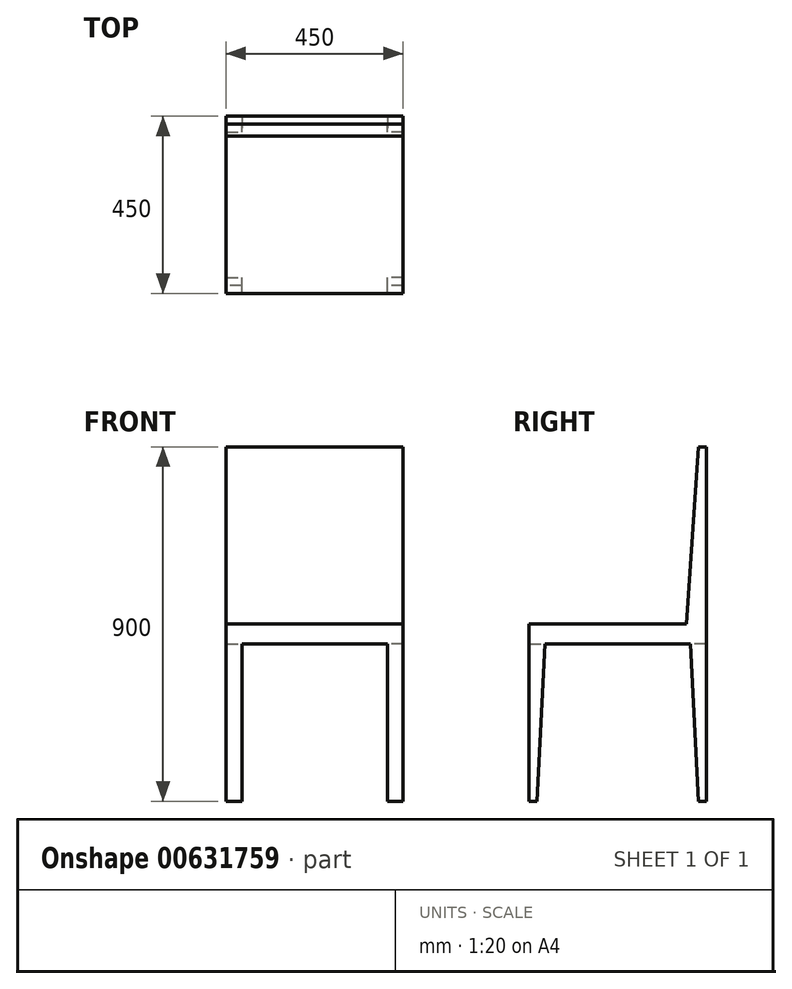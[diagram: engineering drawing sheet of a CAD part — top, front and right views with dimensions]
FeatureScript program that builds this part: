
annotation { "Feature Type Name" : "Feature", "Feature Type Description" : "" }
export const myFeature = defineFeature(function(context is Context, id is Id, definition is map)
    precondition{}
    {
        {
            var Q0;
            Q0=qCreatedBy(makeId("Top.planeOp"),FACE);
            var sketch = newSketch(context, id + "F0", { "sketchPlane" : qUnion([Q0])});
            skLineSegment(sketch, "E0.bottom", {"start": v(0, 0) * mm, "end": v(450, 0) * mm});
            skLineSegment(sketch, "E0.top", {"start": v(0, 450) * mm, "end": v(450, 450) * mm});
            skLineSegment(sketch, "E0.left", {"start": v(0, 0) * mm, "end": v(0, 450) * mm});
            skLineSegment(sketch, "E0.right", {"start": v(450, 0) * mm, "end": v(450, 450) * mm});
            skSolve(sketch);
        }
        {
            var Q0;
            Q0=makeQuery(id+"F0.imprint","IMPRINT",FACE,{"disambiguationData":[TD([[makeQuery(id+"F0.imprint","IMPRINT",EDGE,{"derivedFrom":sQuery(id+"F0.wireOp",EDGE,"E0.bottom")}),1.0]])]});
            extrude(context, id + "F1", {"entities" : qUnion([Q0]), "depth" : 50 * mm, "offsetDistance" : 25 * mm});
        }
        {
            var Q0;
            Q0=makeQuery(id+"F1.opExtrude","CAP_FACE",FACE,{"disambiguationData":[OSD([sQuery(id+"F0.wireOp",EDGE,"E0.bottom"),sQuery(id+"F0.wireOp",EDGE,"E0.top"),sQuery(id+"F0.wireOp",EDGE,"E0.left"),sQuery(id+"F0.wireOp",EDGE,"E0.right")])],"isStart":true});
            var sketch = newSketch(context, id + "F2", { "sketchPlane" : qUnion([Q0])});
            skLineSegment(sketch, "E1.bottom", {"start": v(0, -450) * mm, "end": v(40, -450) * mm});
            skLineSegment(sketch, "E1.top", {"start": v(0, -410) * mm, "end": v(40, -410) * mm});
            skLineSegment(sketch, "E1.left", {"start": v(0, -450) * mm, "end": v(0, -410) * mm});
            skLineSegment(sketch, "E1.right", {"start": v(40, -450) * mm, "end": v(40, -410) * mm});
            skSolve(sketch);
        }
        {
            var Q0;
            Q0=makeQuery(id+"F2.imprint","IMPRINT",FACE,{"disambiguationData":[TD([[makeQuery(id+"F2.imprint","IMPRINT",EDGE,{"derivedFrom":sQuery(id+"F2.wireOp",EDGE,"E1.bottom")}),1.0]])]});
            var Q1;
            Q1=sQuery(id+"F2.wireOp",EDGE,"E1.right");
            extrude(context, id + "F3", {"entities" : qUnion([Q0]), "operationType" : NewBodyOperationType.ADD, "surfaceEntities" : qUnion([Q1]), "depth" : 400 * mm, "offsetDistance" : 25 * mm});
        }
        {
            var Q0;
            Q0=makeQuery(id+"F1.opExtrude","CAP_FACE",FACE,{"disambiguationData":[OSD([sQuery(id+"F0.wireOp",EDGE,"E0.bottom"),sQuery(id+"F0.wireOp",EDGE,"E0.top"),sQuery(id+"F0.wireOp",EDGE,"E0.left"),sQuery(id+"F0.wireOp",EDGE,"E0.right")])],"isStart":true});
            var sketch = newSketch(context, id + "F4", { "sketchPlane" : qUnion([Q0])});
            skLineSegment(sketch, "E2.bottom", {"start": v(0, 0) * mm, "end": v(40, 0) * mm});
            skLineSegment(sketch, "E2.top", {"start": v(0, -40) * mm, "end": v(40, -40) * mm});
            skLineSegment(sketch, "E2.left", {"start": v(0, 0) * mm, "end": v(0, -40) * mm});
            skLineSegment(sketch, "E2.right", {"start": v(40, 0) * mm, "end": v(40, -40) * mm});
            skSolve(sketch);
        }
        {
            var Q0;
            Q0=makeQuery(id+"F4.imprint","IMPRINT",FACE,{"disambiguationData":[TD([[makeQuery(id+"F4.imprint","IMPRINT",EDGE,{"derivedFrom":sQuery(id+"F4.wireOp",EDGE,"E2.bottom")}),-1.0]])]});
            extrude(context, id + "F5", {"entities" : qUnion([Q0]), "operationType" : NewBodyOperationType.ADD, "depth" : 400 * mm, "offsetDistance" : 25 * mm});
        }
        {
            var Q0;
            Q0=makeQuery(id+"F1.opExtrude","CAP_FACE",FACE,{"disambiguationData":[OSD([sQuery(id+"F0.wireOp",EDGE,"E0.bottom"),sQuery(id+"F0.wireOp",EDGE,"E0.top"),sQuery(id+"F0.wireOp",EDGE,"E0.left"),sQuery(id+"F0.wireOp",EDGE,"E0.right")])],"isStart":true});
            var sketch = newSketch(context, id + "F6", { "sketchPlane" : qUnion([Q0])});
            skLineSegment(sketch, "E3.bottom", {"start": v(450, -450) * mm, "end": v(410, -450) * mm});
            skLineSegment(sketch, "E3.top", {"start": v(450, -410) * mm, "end": v(410, -410) * mm});
            skLineSegment(sketch, "E3.left", {"start": v(450, -450) * mm, "end": v(450, -410) * mm});
            skLineSegment(sketch, "E3.right", {"start": v(410, -450) * mm, "end": v(410, -410) * mm});
            skSolve(sketch);
        }
        {
            var Q0;
            Q0=qSketchRegion(id+"F6",true);
            var Q1;
            Q1=makeQuery(id+"F6.imprint","IMPRINT",FACE,{"disambiguationData":[TD([[makeQuery(id+"F6.imprint","IMPRINT",EDGE,{"derivedFrom":sQuery(id+"F6.wireOp",EDGE,"E3.bottom")}),1.0]])]});
            extrude(context, id + "F7", {"entities" : qUnion([Q0, Q1]), "operationType" : NewBodyOperationType.ADD, "depth" : 400 * mm, "offsetDistance" : 25 * mm});
        }
        {
            var Q0;
            Q0=makeQuery(id+"F1.opExtrude","CAP_FACE",FACE,{"disambiguationData":[OSD([sQuery(id+"F0.wireOp",EDGE,"E0.bottom"),sQuery(id+"F0.wireOp",EDGE,"E0.top"),sQuery(id+"F0.wireOp",EDGE,"E0.left"),sQuery(id+"F0.wireOp",EDGE,"E0.right")])],"isStart":true});
            var sketch = newSketch(context, id + "F8", { "sketchPlane" : qUnion([Q0])});
            skLineSegment(sketch, "E4.bottom", {"start": v(450, 0) * mm, "end": v(410, 0) * mm});
            skLineSegment(sketch, "E4.top", {"start": v(450, -40) * mm, "end": v(410, -40) * mm});
            skLineSegment(sketch, "E4.left", {"start": v(450, 0) * mm, "end": v(450, -40) * mm});
            skLineSegment(sketch, "E4.right", {"start": v(410, 0) * mm, "end": v(410, -40) * mm});
            skSolve(sketch);
        }
        {
            var Q0;
            Q0=makeQuery(id+"F8.imprint","IMPRINT",FACE,{"disambiguationData":[TD([[makeQuery(id+"F8.imprint","IMPRINT",EDGE,{"derivedFrom":sQuery(id+"F8.wireOp",EDGE,"E4.bottom")}),-1.0]])]});
            extrude(context, id + "F9", {"entities" : qUnion([Q0]), "operationType" : NewBodyOperationType.ADD, "depth" : 400 * mm, "offsetDistance" : 25 * mm});
        }
        {
            var Q0;
            Q0=makeQuery(id+"F1.opExtrude","CAP_FACE",FACE,{"disambiguationData":[OSD([sQuery(id+"F0.wireOp",EDGE,"E0.bottom"),sQuery(id+"F0.wireOp",EDGE,"E0.top"),sQuery(id+"F0.wireOp",EDGE,"E0.left"),sQuery(id+"F0.wireOp",EDGE,"E0.right")])],"isStart":false});
            var sketch = newSketch(context, id + "F10", { "sketchPlane" : qUnion([Q0])});
            skLineSegment(sketch, "E5.bottom", {"start": v(450, 450) * mm, "end": v(0, 450) * mm});
            skLineSegment(sketch, "E5.top", {"start": v(450, 400) * mm, "end": v(0, 400) * mm});
            skLineSegment(sketch, "E5.left", {"start": v(450, 450) * mm, "end": v(450, 400) * mm});
            skLineSegment(sketch, "E5.right", {"start": v(0, 450) * mm, "end": v(0, 400) * mm});
            skSolve(sketch);
        }
        {
            var Q0;
            Q0=makeQuery(id+"F10.imprint","IMPRINT",FACE,{"disambiguationData":[TD([[makeQuery(id+"F10.imprint","IMPRINT",EDGE,{"derivedFrom":sQuery(id+"F10.wireOp",EDGE,"E5.bottom")}),-1.0]])]});
            extrude(context, id + "F11", {"entities" : qUnion([Q0]), "operationType" : NewBodyOperationType.ADD, "depth" : 450 * mm, "offsetDistance" : 25 * mm});
        }
        {
            var Q0;
            Q0=makeQuery(id+"F11.boolean.opBoolean","MERGE",FACE,{"derivedFrom":[makeQuery(id+"F9.boolean.opBoolean","MERGE",FACE,{"derivedFrom":[makeQuery(id+"F7.boolean.opBoolean","MERGE",FACE,{"derivedFrom":[makeQuery(id+"F1.opExtrude","SWEPT_FACE",FACE,{"disambiguationData":[OSD([sQuery(id+"F0.wireOp",EDGE,"E0.right")])]}),makeQuery(id+"F7.opExtrude","SWEPT_FACE",FACE,{"disambiguationData":[OSD([sQuery(id+"F6.wireOp",EDGE,"E3.left")])]})]}),makeQuery(id+"F9.opExtrude","SWEPT_FACE",FACE,{"disambiguationData":[OSD([sQuery(id+"F8.wireOp",EDGE,"E4.left")])]})]}),makeQuery(id+"F11.opExtrude","SWEPT_FACE",FACE,{"disambiguationData":[OSD([sQuery(id+"F10.wireOp",EDGE,"E5.left")])]})]});
            var sketch = newSketch(context, id + "F12", { "sketchPlane" : qUnion([Q0])});
            skLineSegment(sketch, "E6", {"start": v(400, 50) * mm, "end": v(430, 500) * mm});
            skLineSegment(sketch, "E7", {"start": v(430, 500) * mm, "end": v(400, 500) * mm});
            skLineSegment(sketch, "E8", {"start": v(400, 500) * mm, "end": v(400, 50) * mm});
            skSolve(sketch);
        }
        {
            var Q0;
            Q0=makeQuery(id+"F12.imprint","IMPRINT",FACE,{"disambiguationData":[TD([[makeQuery(id+"F12.imprint","IMPRINT",EDGE,{"derivedFrom":sQuery(id+"F12.wireOp",EDGE,"E6")}),1.0]])]});
            extrude(context, id + "F13", {"entities" : qUnion([Q0]), "operationType" : NewBodyOperationType.REMOVE, "oppositeDirection" : true, "depth" : 450 * mm, "offsetDistance" : 25 * mm});
        }
        {
            var Q0;
            Q0=makeQuery(id+"F11.boolean.opBoolean","MERGE",FACE,{"derivedFrom":[makeQuery(id+"F5.boolean.opBoolean","MERGE",FACE,{"derivedFrom":[makeQuery(id+"F3.boolean.opBoolean","MERGE",FACE,{"derivedFrom":[makeQuery(id+"F1.opExtrude","SWEPT_FACE",FACE,{"disambiguationData":[OSD([sQuery(id+"F0.wireOp",EDGE,"E0.left")])]}),makeQuery(id+"F3.opExtrude","SWEPT_FACE",FACE,{"disambiguationData":[OSD([sQuery(id+"F2.wireOp",EDGE,"E1.left")])]})]}),makeQuery(id+"F5.opExtrude","SWEPT_FACE",FACE,{"disambiguationData":[OSD([sQuery(id+"F4.wireOp",EDGE,"E2.left")])]})]}),makeQuery(id+"F11.opExtrude","SWEPT_FACE",FACE,{"disambiguationData":[OSD([sQuery(id+"F10.wireOp",EDGE,"E5.right")])]})]});
            var sketch = newSketch(context, id + "F14", { "sketchPlane" : qUnion([Q0])});
            skLineSegment(sketch, "E9", {"start": v(-410, 0) * mm, "end": v(-430, -400) * mm});
            skLineSegment(sketch, "E10", {"start": v(-430, -400) * mm, "end": v(-410, -400) * mm});
            skLineSegment(sketch, "E11", {"start": v(-410, -400) * mm, "end": v(-410, 0) * mm});
            skSolve(sketch);
        }
        {
            var Q0;
            Q0=makeQuery(id+"F14.imprint","IMPRINT",FACE,{"disambiguationData":[TD([[makeQuery(id+"F14.imprint","IMPRINT",EDGE,{"derivedFrom":sQuery(id+"F14.wireOp",EDGE,"E9")}),1.0]])]});
            extrude(context, id + "F15", {"entities" : qUnion([Q0]), "operationType" : NewBodyOperationType.REMOVE, "endBound" : BoundingType.THROUGH_ALL, "oppositeDirection" : true, "depth" : 25 * mm, "offsetDistance" : 25 * mm});
        }
        {
            var Q0;
            Q0=makeQuery(id+"F11.boolean.opBoolean","MERGE",FACE,{"derivedFrom":[makeQuery(id+"F5.boolean.opBoolean","MERGE",FACE,{"derivedFrom":[makeQuery(id+"F3.boolean.opBoolean","MERGE",FACE,{"derivedFrom":[makeQuery(id+"F1.opExtrude","SWEPT_FACE",FACE,{"disambiguationData":[OSD([sQuery(id+"F0.wireOp",EDGE,"E0.left")])]}),makeQuery(id+"F3.opExtrude","SWEPT_FACE",FACE,{"disambiguationData":[OSD([sQuery(id+"F2.wireOp",EDGE,"E1.left")])]})]}),makeQuery(id+"F5.opExtrude","SWEPT_FACE",FACE,{"disambiguationData":[OSD([sQuery(id+"F4.wireOp",EDGE,"E2.left")])]})]}),makeQuery(id+"F11.opExtrude","SWEPT_FACE",FACE,{"disambiguationData":[OSD([sQuery(id+"F10.wireOp",EDGE,"E5.right")])]})]});
            var sketch = newSketch(context, id + "F16", { "sketchPlane" : qUnion([Q0])});
            skLineSegment(sketch, "E12", {"start": v(-40, 0) * mm, "end": v(-20, -400) * mm});
            skLineSegment(sketch, "E13", {"start": v(-20, -400) * mm, "end": v(-40, -400) * mm});
            skLineSegment(sketch, "E14", {"start": v(-40, -400) * mm, "end": v(-40, 0) * mm});
            skSolve(sketch);
        }
        {
            var Q0;
            Q0=makeQuery(id+"F16.imprint","IMPRINT",FACE,{"disambiguationData":[TD([[makeQuery(id+"F16.imprint","IMPRINT",EDGE,{"derivedFrom":sQuery(id+"F16.wireOp",EDGE,"E12")}),-1.0]])]});
            extrude(context, id + "F17", {"entities" : qUnion([Q0]), "operationType" : NewBodyOperationType.REMOVE, "endBound" : BoundingType.THROUGH_ALL, "oppositeDirection" : true, "depth" : 25 * mm, "offsetDistance" : 25 * mm});
        }
        {
            var Q0;
            Q0=makeQuery(id+"F1.opExtrude","CAP_FACE",FACE,{"disambiguationData":[OSD([sQuery(id+"F0.wireOp",EDGE,"E0.bottom"),sQuery(id+"F0.wireOp",EDGE,"E0.top"),sQuery(id+"F0.wireOp",EDGE,"E0.left"),sQuery(id+"F0.wireOp",EDGE,"E0.right")])],"isStart":false});
            extrude(context, id + "F18", {"entities" : qUnion([Q0]), "operationType" : NewBodyOperationType.ADD, "depth" : 100 * mm, "offsetDistance" : 25 * mm});
        }
        {
            var Q0;
            Q0=makeQuery(id+"F18.opExtrude","CAP_FACE",FACE,{"disambiguationData":[OSD([sQuery(id+"F0.wireOp",EDGE,"E0.bottom"),sQuery(id+"F0.wireOp",EDGE,"E0.top"),sQuery(id+"F0.wireOp",EDGE,"E0.left"),sQuery(id+"F0.wireOp",EDGE,"E0.right")])],"isStart":false});
            extrude(context, id + "F19", {"entities" : qUnion([Q0]), "operationType" : NewBodyOperationType.REMOVE, "oppositeDirection" : true, "depth" : 100 * mm, "offsetDistance" : 25 * mm});
        }
        {
            var Q0;
            Q0=makeQuery(id+"F19.boolean.opBoolean","COPY",FACE,{"derivedFrom":makeQuery(id+"F19.opExtrude","CAP_FACE",FACE,{"disambiguationData":[OSD([sQuery(id+"F0.wireOp",EDGE,"E0.bottom"),sQuery(id+"F0.wireOp",EDGE,"E0.top"),sQuery(id+"F0.wireOp",EDGE,"E0.left"),sQuery(id+"F0.wireOp",EDGE,"E0.right")])],"isStart":false})});
            extrude(context, id + "F20", {"entities" : qUnion([Q0]), "operationType" : NewBodyOperationType.ADD, "depth" : 200 * mm, "offsetDistance" : 25 * mm});
        }
        {
            var Q0;
            Q0=makeQuery(id+"F20.opExtrude","CAP_FACE",FACE,{"disambiguationData":[OSD([sQuery(id+"F0.wireOp",EDGE,"E0.bottom"),sQuery(id+"F0.wireOp",EDGE,"E0.top"),sQuery(id+"F0.wireOp",EDGE,"E0.left"),sQuery(id+"F0.wireOp",EDGE,"E0.right")])],"isStart":false});
            extrude(context, id + "F21", {"entities" : qUnion([Q0]), "operationType" : NewBodyOperationType.REMOVE, "oppositeDirection" : true, "depth" : 200 * mm, "offsetDistance" : 25 * mm});
        }
    });
